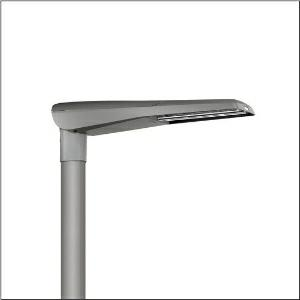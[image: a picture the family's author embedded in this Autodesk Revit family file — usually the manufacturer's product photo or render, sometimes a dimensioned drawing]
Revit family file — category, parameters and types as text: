
# Revit family: streetlight_sl_11_iq_mini___st1_2a_5xc2ac1f08he_c396
name_source: partatom
category: Lighting Fixtures
units: mm (PartAtom-declared; Revit-internal decimal feet)

## family parameters
Cut with Voids When Loaded = No
Host = Face
Light Source = No
Part Type = Normal
Room Calculation Point = No
Round Connector Dimension = Use Diameter
Shared = No

## types (1)
- --- (1 x LED, 6820 lm, 63.6 W, 2200K)
    Apparent Load = 64 VA
    CIE Flux Codes = 32 70 96 100 100
    Color Rendering = 70
    Color Temperature = 2200K
    Default Elevation = 1800 mm
    Description = Streetlight SL 11 iQ mini, mast luminaire, primary light control with 3 zone facetted reflector, of plastic, silver coated, highly specular, primary optical cover: cover, of PMMA, transparent, light distribution: ST1.2a, light emission: direct distribution, primary light characteristic: asymmetric, installation type: post-top, side-entry, LED, High Power LED, rated luminous flux: 8.330lm, luminous efficacy: 134lm/W, light colour: 722/727/730/740, colour temperature: 2200/2700/3000/4000K, control gear: iQ Street-Remote, control: Street-Remote, Auto-Match, Temp-Guard, Lumen-Switch, Night-Set, Smart-Wire, Light-Fading, Desk-Remote (wireless, voltage-free reading and setting of iQ features in the workshop via application-optimized NFC function/RFID function), optimised constant luminous flux control (CLO 2.0), with cable H07RN-F 5x 1.5mm², mains connection: 230..240V, AC, 50/60Hz, connection cable pre-assembled, cable length: 8,5m, start of lifetime: 62W, end of service life: 66W, reduction: 29W, luminaire housing, of diecast aluminium, powder-coated, Siteco® metallic grey (DB 702S), please order mast flange separately, inclination adjustable without tools: 0°, 5°, 10°, 15° (post-top) | 0°, -5°, -10°, -15° (side-entry), sealing non-destructively replaceable, multi-level sealing system, length: 736mm, width: 174mm, height: 116mm, mast flange for spigot size: 42mm (side-entry): 5XC10008XM4, 60/48mm (side-entry/post-top): 5XC10108XM2, 76/60mm (side-entry/post-top): 5XC10108XM1, mounting height: 4..8m, equipment: Power, protection rating (complete): IP66, insulation class (complete): insulation class II (safety insulation), certification: CE, ENEC, VDE, impact resistance: IK09, permissible operating ambient temperature for outdoor applications: -25..+50°C, standard-compliant lighting for roads and squares, Environmental Product Declaration (EPD) tested and certified by an independent institute, packaging unit: 1 piece

Light Distribution: ST1.2a
    Height = 116 mm
    Lamp = 1 x LED
    Lamp Light Flux = 6820 lm
    Lamp Power = 63.6 W
    Lamp count = 1
    Length = 736 mm
    Luminous efficacy = 107 lm/W
    Manufacturer = Siteco
    ModVariant = No
    Model = 5XC2AC1F08HE
    Number of Poles = 1
    OnlyDefault = Yes
    Power Factor = 1
    Product Name = Streetlight SL 11 iQ mini | ST1.2a
    Product group = mast luminaire | pylon top
    ProductGroupID = 6100
    Protection Class = Protection class II
    Protection Degree = IP 66
    RLX_Detail_Level = 1
    RLX_Emergency_Light_Flux = 0 lm
    RLX_Emergency_Type = 0
    RLX_Emergency_Type_DB = No
    RlxData = <blob elided: 53673 chars, md5=97092574>
    Socket = socket
    Standby Power = 0 W
    System Light Flux = 6820 lm
    System Power = 64 W
    Type Comments = individual setting: luminous flux: 100 % | dim-lin: 254 | 866 mA
    Type Image = l_1003508.jpg
    URL = http://relux.com
    VarID = @adj_031434
    Voltage = 0 V
    Weight = 0.00 kg
    Width = 174 mm

## geometry (parser evidence)
native form markers: Blend x4, Sweep x13
no freeform markers — native parametric forms only
